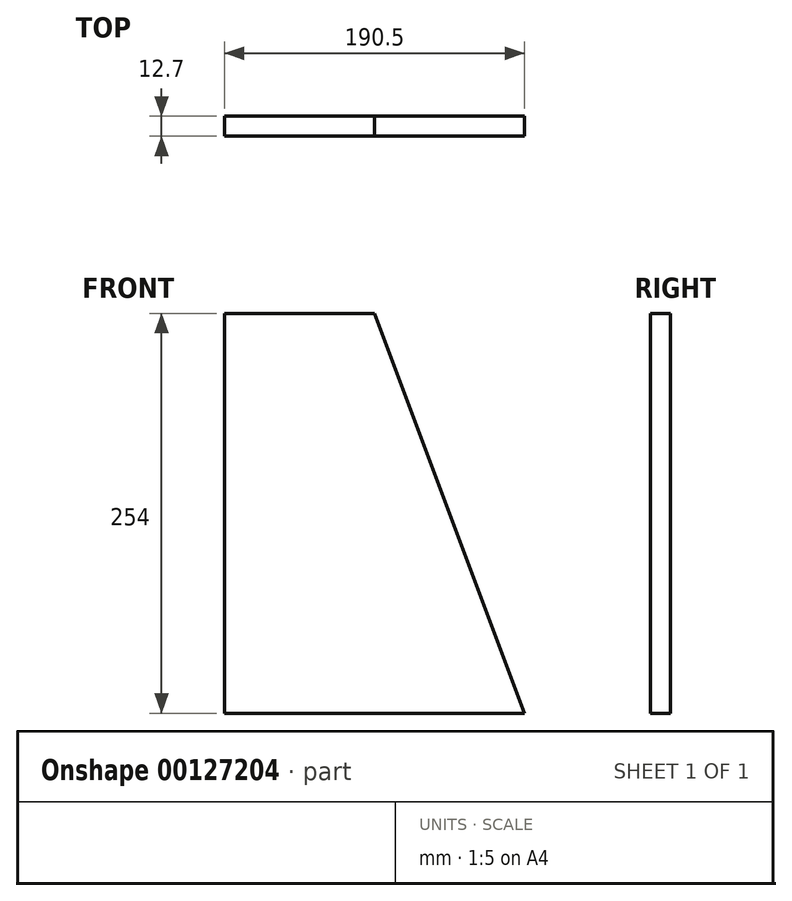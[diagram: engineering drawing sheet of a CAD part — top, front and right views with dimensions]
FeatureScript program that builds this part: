
annotation { "Feature Type Name" : "Feature", "Feature Type Description" : "" }
export const myFeature = defineFeature(function(context is Context, id is Id, definition is map)
    precondition{}
    {
        {
            var Q0;
            Q0=qCreatedBy(makeId("Front.planeOp"),FACE);
            var sketch = newSketch(context, id + "F0", { "sketchPlane" : qUnion([Q0])});
            skLineSegment(sketch, "E0.bottom", {"start": v(95.25, 127) * mm, "end": v(-95.25, 127) * mm});
            skLineSegment(sketch, "E0.top", {"start": v(95.25, -127) * mm, "end": v(-95.25, -127) * mm});
            skLineSegment(sketch, "E0.left", {"start": v(95.25, 127) * mm, "end": v(95.25, -127) * mm});
            skLineSegment(sketch, "E0.right", {"start": v(-95.25, 127) * mm, "end": v(-95.25, -127) * mm});
            skPoint(sketch, "E0.middle", {"position": v(0, 0) * mm});
            skLineSegment(sketch, "E1", {"start": v(0, 127) * mm, "end": v(95.25, -127) * mm});
            skSolve(sketch);
        }
        {
            var Q0;
            Q0=makeQuery(id+"F0.imprint","IMPRINT",FACE,{"disambiguationData":[TD([[makeQuery(id+"F0.imprint","IMPRINT",EDGE,{"derivedFrom":sQuery(id+"F0.wireOp",EDGE,"E0.top")}),-1.0]])]});
            extrude(context, id + "F1", {"entities" : qUnion([Q0]), "depth" : 12.7 * mm});
        }
    });
